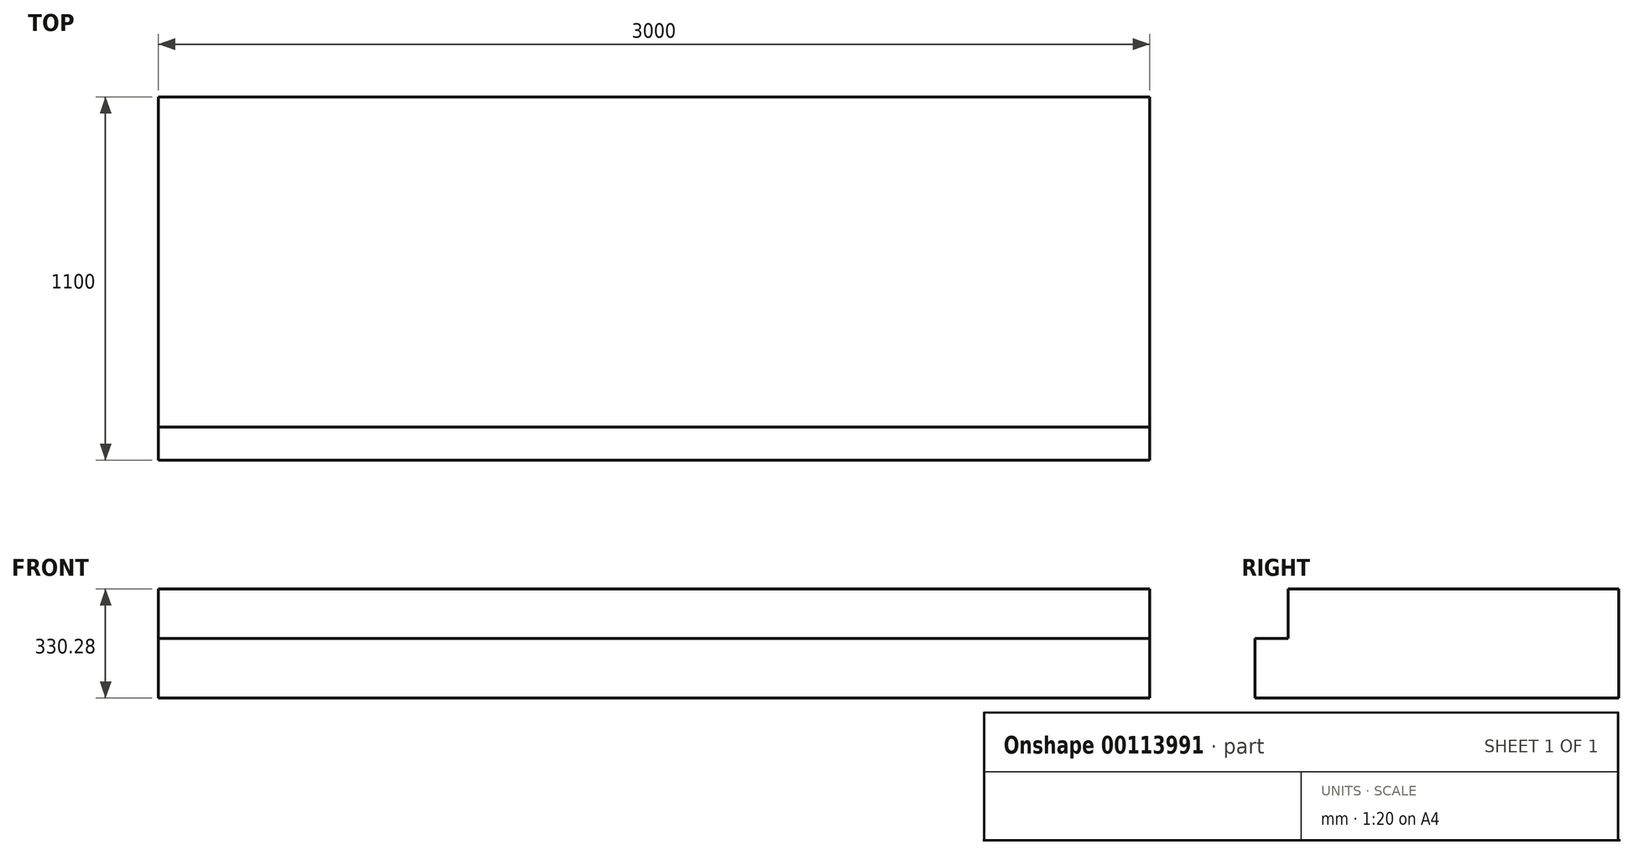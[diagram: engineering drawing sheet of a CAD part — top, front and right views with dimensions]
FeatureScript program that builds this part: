
annotation { "Feature Type Name" : "Feature", "Feature Type Description" : "" }
export const myFeature = defineFeature(function(context is Context, id is Id, definition is map)
    precondition{}
    {
        {
            var Q0;
            Q0=qCreatedBy(makeId("Top.planeOp"),FACE);
            var sketch = newSketch(context, id + "F0", { "sketchPlane" : qUnion([Q0])});
            skLineSegment(sketch, "E0.bottom", {"start": v(-1500, 2000) * mm, "end": v(1500, 2000) * mm});
            skLineSegment(sketch, "E0.top", {"start": v(-1500, -2000) * mm, "end": v(1500, -2000) * mm});
            skLineSegment(sketch, "E0.left", {"start": v(-1500, 2000) * mm, "end": v(-1500, -2000) * mm});
            skLineSegment(sketch, "E0.right", {"start": v(1500, 2000) * mm, "end": v(1500, -2000) * mm});
            skPoint(sketch, "E0.middle", {"position": v(0, 0) * mm});
            skSolve(sketch);
        }
        {
            var Q0;
            Q0=qCreatedBy(makeId("Right.planeOp"),FACE);
            var sketch = newSketch(context, id + "F1", { "sketchPlane" : qUnion([Q0])});
            skLineSegment(sketch, "E1", {"start": v(2000, 0) * mm, "end": v(2000, -330.28) * mm});
            skLineSegment(sketch, "E2", {"start": v(2000, -330.28) * mm, "end": v(1800, -330.28) * mm});
            skLineSegment(sketch, "E3", {"start": v(2000, 0) * mm, "end": v(1900, 0) * mm});
            skLineSegment(sketch, "E4", {"start": v(1900, 0) * mm, "end": v(1900, -150) * mm});
            skLineSegment(sketch, "E5", {"start": v(1900, -150) * mm, "end": v(1800, -150) * mm});
            skLineSegment(sketch, "E6", {"start": v(1800, -150) * mm, "end": v(1800, -330.28) * mm});
            skLineSegment(sketch, "E7", {"start": v(1900, 0) * mm, "end": v(1000, 0) * mm});
            skLineSegment(sketch, "E8", {"start": v(1000, 0) * mm, "end": v(1000, -150) * mm});
            skLineSegment(sketch, "E9", {"start": v(1000, -150) * mm, "end": v(900, -150) * mm});
            skLineSegment(sketch, "E10", {"start": v(900, -150) * mm, "end": v(900, -330.28) * mm});
            skLineSegment(sketch, "E11", {"start": v(900, -330.28) * mm, "end": v(1800, -330.28) * mm});
            skLineSegment(sketch, "E12", {"start": v(1800, -150) * mm, "end": v(1000, -150) * mm});
            skSolve(sketch);
        }
        {
            var Q0;
            Q0=makeQuery(id+"F1.imprint","IMPRINT",FACE,{"disambiguationData":[TD([[makeQuery(id+"F1.imprint","IMPRINT",EDGE,{"derivedFrom":sQuery(id+"F1.wireOp",EDGE,"E1")}),-1.0]])]});
            var Q1;
            Q1=makeQuery(id+"F1.imprint","IMPRINT",FACE,{"disambiguationData":[TD([[makeQuery(id+"F1.imprint","IMPRINT",EDGE,{"derivedFrom":sQuery(id+"F1.wireOp",EDGE,"E4")}),-1.0]])]});
            var Q2;
            Q2=makeQuery(id+"F1.imprint","IMPRINT",FACE,{"disambiguationData":[TD([[makeQuery(id+"F1.imprint","IMPRINT",EDGE,{"derivedFrom":sQuery(id+"F1.wireOp",EDGE,"E6")}),-1.0]])]});
            extrude(context, id + "F2", {"entities" : qUnion([Q0, Q1, Q2]), "endBound" : BoundingType.SYMMETRIC, "depth" : 3000 * mm});
        }
    });
